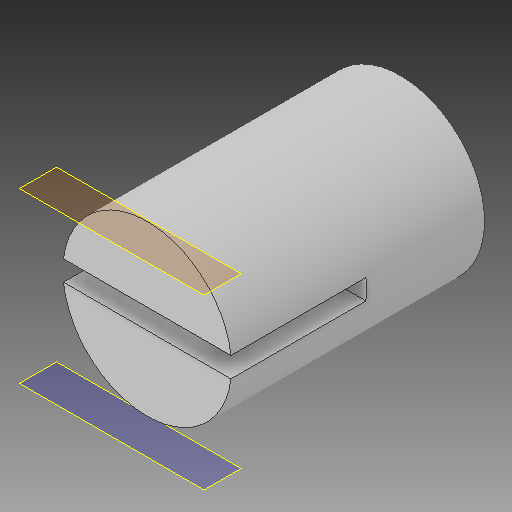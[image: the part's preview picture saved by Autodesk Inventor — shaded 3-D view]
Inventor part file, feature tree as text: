
AUTODESK INVENTOR PART (.ipt)
format: ipt  version: 2019 (Build 230136000, 136)  size: 149,504 bytes
history: native  units: mm
features: sketch x6, extrude x4, hole x2, plane x2
ambient origin geometry x8: Origin, YZ Plane, XZ Plane, XY Plane, X Axis, Y Axis, Z Axis, Center Point
bodies: Solid1 (feature_tree)
feature tree (14):
  extrude  "Extrusion1"  Depth=15.0mm TaperAngle=0.0deg
  sketch  "Sketch2"  dims[d3=1.0mm]
  hole  "Hole1"  [1 undecoded]
  extrude  "Extrusion2"  Depth=4.5mm
  plane  "Work Plane1"
  plane  "Work Plane2"
  hole  "Hole2"  [1 undecoded]
  extrude  "Extrusion3"  Depth=10.0mm TaperAngle=0.0deg
  extrude  "Extrusion4"  Depth=1.2mm
  sketch  "Sketch1"  dims[d0=10.0mm d1=15.0mm d2=0.0mm]
  sketch  "Sketch3"  dims[d4=3.302mm d5=5.0mm d6=4.0mm d7=2.0mm d8=90.0deg d9=7.0mm d10=0.0mm d11=2.0mm d12=0.0mm]
  sketch  "Sketch5"  dims[d13=4.5mm d15=4.5mm]
  sketch  "Sketch6"  dims[d16=4.0mm]
  sketch  "Sketch7"  dims[d17=3.302mm d18=4.5mm d19=4.0mm d20=2.0mm d21=90.0deg d22=4.5mm d23=0.0mm d31=2.0mm d32=0.0mm d33=10.0mm d34=0.0mm d35=1.2mm d36=0.6mm d37=1.0mm d38=1.0mm]
note: 2 required parameter values undecoded (feature->parameter linkage not recoverable at this tier; creation-order binding heuristic only, values carry confidence <= 0.55)
